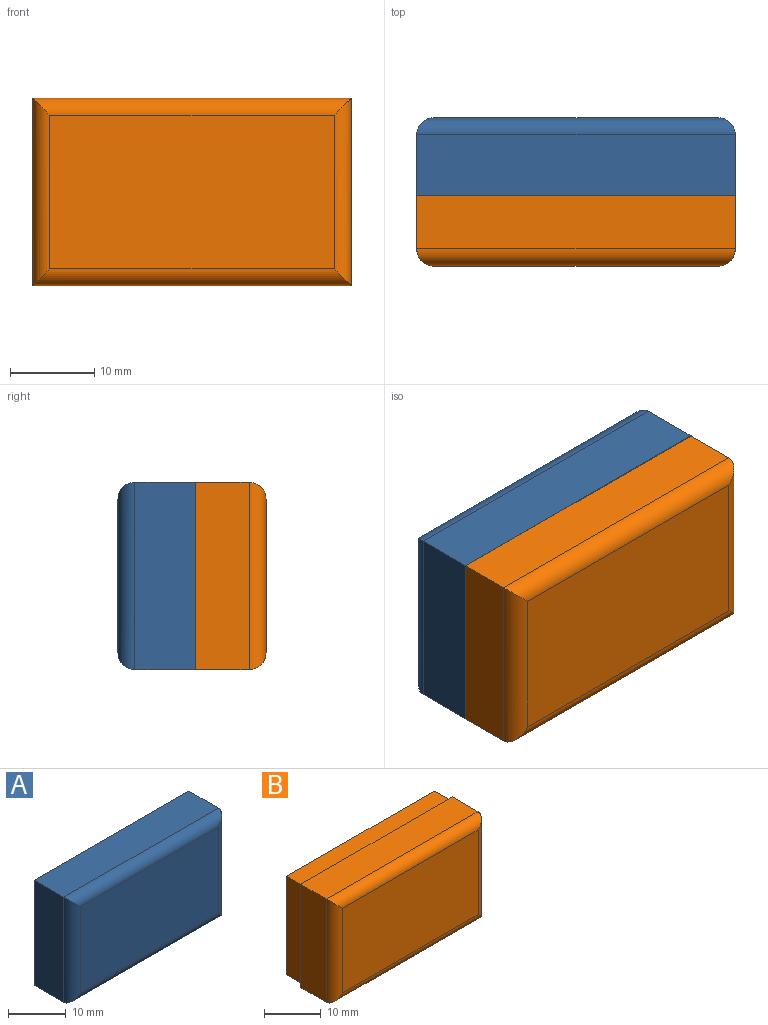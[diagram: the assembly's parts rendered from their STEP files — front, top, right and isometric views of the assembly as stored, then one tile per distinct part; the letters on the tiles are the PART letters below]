
ASSEMBLY  parts=2 mates=1
PART A: 24 faces, bbox 37.8x9.2x22.2 mm
  f0: plane 36.77x21.24mm, normal (0,1,0), area 57mm2, adj f1,f2,f3,f4,f10,f11,f12,f13
  f1: plane 20.24x4.2mm, normal (1,0,0), area 85mm2, adj f0,f2,f4,f6
  f2: plane 35.77x4.2mm, normal (0,0,1), area 150.2mm2, adj f0,f1,f3,f7
  f3: plane 20.24x4.2mm, normal (-1,0,0), area 85mm2, adj f0,f2,f4,f9
  f4: plane 35.77x4.2mm, normal (0,0,-1), area 150.2mm2, adj f0,f1,f3,f8
  f5: plane 33.77x18.24mm, normal (0,1,0), area 616mm2, adj f6,f7,f8,f9
  f6: cylinder r=1mm len=20.24mm, axis (0,0,1), area 30.7mm2, adj f1,f5,f7,f8
  f7: cylinder r=1mm len=35.77mm, axis (-1,0,0), area 55mm2, adj f2,f5,f6,f9
  f8: cylinder r=1mm len=35.77mm, axis (1,0,0), area 55mm2, adj f4,f5,f6,f9
  f9: cylinder r=1mm len=20.24mm, axis (0,0,-1), area 30.7mm2, adj f3,f5,f7,f8
  f10: plane 36.77x3mm, normal (0,0,-1), area 110.3mm2, adj f0,f11,f13,f14
  f11: plane 21.24x3mm, normal (1,0,0), area 63.7mm2, adj f0,f10,f12,f14
  f12: plane 36.77x3mm, normal (0,0,1), area 110.3mm2, adj f0,f11,f13,f14
  f13: plane 21.24x3mm, normal (-1,0,0), area 63.7mm2, adj f0,f10,f12,f14
  f14: plane 37.77x22.24mm, normal (0,1,0), area 59mm2, adj f10,f11,f12,f13,f20,f21,f22,f23
  f15: plane 33.77x18.24mm, normal (0,-1,0), area 616mm2, adj f16,f17,f18,f19
  f16: cylinder r=2mm len=22.24mm, axis (0,0,1), area 65.3mm2, adj f15,f17,f19,f23
  f17: cylinder r=2mm len=37.77mm, axis (1,0,0), area 114.1mm2, adj f15,f16,f18,f22
  f18: cylinder r=2mm len=22.24mm, axis (0,0,-1), area 65.3mm2, adj f15,f17,f19,f21
  f19: cylinder r=2mm len=37.77mm, axis (-1,0,0), area 114.1mm2, adj f15,f16,f18,f20
  f20: plane 37.77x7.2mm, normal (0,0,-1), area 271.9mm2, adj f14,f19,f21,f23
  f21: plane 22.24x7.2mm, normal (1,0,0), area 160.2mm2, adj f14,f18,f20,f22
  f22: plane 37.77x7.2mm, normal (0,0,1), area 271.9mm2, adj f14,f17,f21,f23
  f23: plane 22.24x7.2mm, normal (-1,0,0), area 160.2mm2, adj f14,f16,f20,f22
PART B: 24 faces, bbox 37.8x12.4x22.2 mm
  f0: plane 37.77x22.24mm, normal (0,1,0), area 59mm2, adj f1,f2,f3,f4,f10,f11,f12,f13
  f1: plane 22.24x6.4mm, normal (-1,0,0), area 142.4mm2, adj f0,f2,f4,f6
  f2: plane 37.77x6.4mm, normal (0,0,-1), area 241.7mm2, adj f0,f1,f3,f7
  f3: plane 22.24x6.4mm, normal (1,0,0), area 142.4mm2, adj f0,f2,f4,f9
  f4: plane 37.77x6.4mm, normal (0,0,1), area 241.7mm2, adj f0,f1,f3,f8
  f5: plane 33.77x18.24mm, normal (0,-1,0), area 616mm2, adj f6,f7,f8,f9
  f6: cylinder r=2mm len=22.24mm, axis (0,0,1), area 65.3mm2, adj f1,f5,f7,f8
  f7: cylinder r=2mm len=37.77mm, axis (-1,0,0), area 114.1mm2, adj f2,f5,f6,f9
  f8: cylinder r=2mm len=37.77mm, axis (1,0,0), area 114.1mm2, adj f4,f5,f6,f9
  f9: cylinder r=2mm len=22.24mm, axis (0,0,-1), area 65.3mm2, adj f3,f5,f7,f8
  f10: plane 21.24x4mm, normal (-1,0,0), area 85mm2, adj f0,f11,f13,f14
  f11: plane 36.77x4mm, normal (0,0,1), area 147.1mm2, adj f0,f10,f12,f14
  f12: plane 21.24x4mm, normal (1,0,0), area 85mm2, adj f0,f11,f13,f14
  f13: plane 36.77x4mm, normal (0,0,-1), area 147.1mm2, adj f0,f10,f12,f14
  f14: plane 36.77x21.24mm, normal (0,1,0), area 57mm2, adj f10,f11,f12,f13,f20,f21,f22,f23
  f15: plane 33.77x18.24mm, normal (0,1,0), area 616mm2, adj f16,f17,f18,f19
  f16: cylinder r=1mm len=20.24mm, axis (0,0,1), area 30.7mm2, adj f15,f17,f19,f23
  f17: cylinder r=1mm len=35.77mm, axis (-1,0,0), area 55mm2, adj f15,f16,f18,f22
  f18: cylinder r=1mm len=20.24mm, axis (0,0,-1), area 30.7mm2, adj f15,f17,f19,f21
  f19: cylinder r=1mm len=35.77mm, axis (1,0,0), area 55mm2, adj f15,f16,f18,f20
  f20: plane 35.77x10.4mm, normal (0,0,-1), area 372mm2, adj f14,f19,f21,f23
  f21: plane 20.24x10.4mm, normal (-1,0,0), area 210.5mm2, adj f14,f18,f20,f22
  f22: plane 35.77x10.4mm, normal (0,0,1), area 372mm2, adj f14,f17,f21,f23
  f23: plane 20.24x10.4mm, normal (1,0,0), area 210.5mm2, adj f14,f16,f20,f22
PLACE A rot(axis=(0,0,-1),180deg) t=(16.43,6.08,-9.02)mm
PLACE B rot(axis=(-0.89,0.18,0.41),0deg) t=(-21.33,3.12,-9.02)mm fixed
MATE slider A.f15 <-> B.f15  axis (0,1,0) through (-2.45,12.28,2.1)mm
